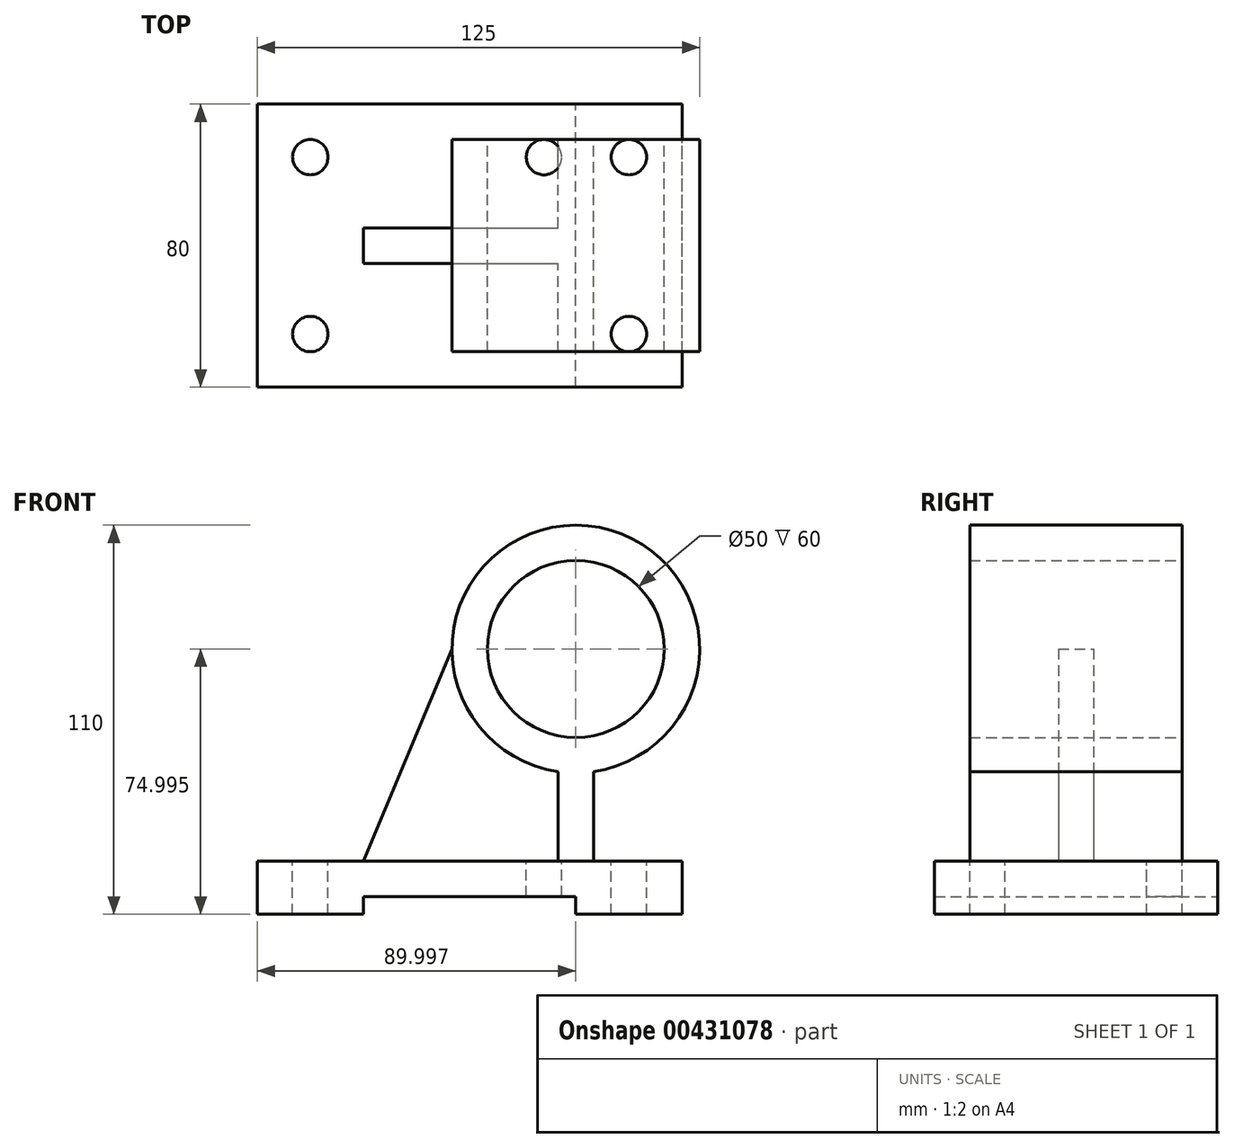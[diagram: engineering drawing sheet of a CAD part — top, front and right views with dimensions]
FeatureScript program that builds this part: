
annotation { "Feature Type Name" : "Feature", "Feature Type Description" : "" }
export const myFeature = defineFeature(function(context is Context, id is Id, definition is map)
    precondition{}
    {
        {
            var Q0;
            Q0=qCreatedBy(makeId("Front.planeOp"),FACE);
            var sketch = newSketch(context, id + "F0", { "sketchPlane" : qUnion([Q0])});
            skLineSegment(sketch, "E0.bottom", {"start": v(-48, -13.36) * mm, "end": v(72, -13.36) * mm});
            skLineSegment(sketch, "E0.top", {"start": v(-48, -28.36) * mm, "end": v(72, -28.36) * mm});
            skLineSegment(sketch, "E0.left", {"start": v(-48, -13.36) * mm, "end": v(-48, -28.36) * mm});
            skLineSegment(sketch, "E0.right", {"start": v(72, -13.36) * mm, "end": v(72, -28.36) * mm});
            skCircle(sketch, "E1", {"center": v(42, 46.64) * mm, "radius": 25 * mm});
            skCircle(sketch, "E2", {"center": v(42, 46.64) * mm, "radius": 35 * mm});
            skLineSegment(sketch, "E3", {"start": v(42, -13.36) * mm, "end": v(37, -13.36) * mm});
            skLineSegment(sketch, "E4", {"start": v(37, -13.36) * mm, "end": v(47, -13.36) * mm});
            skLineSegment(sketch, "E5", {"start": v(47, -13.36) * mm, "end": v(47, 12) * mm});
            skLineSegment(sketch, "E6", {"start": v(37, 12) * mm, "end": v(37, -13.36) * mm});
            skLineSegment(sketch, "E7.bottom", {"start": v(-18, -28.36) * mm, "end": v(42, -28.36) * mm});
            skLineSegment(sketch, "E7.top", {"start": v(-18, -23.36) * mm, "end": v(42, -23.36) * mm});
            skLineSegment(sketch, "E7.left", {"start": v(-18, -28.36) * mm, "end": v(-18, -23.36) * mm});
            skLineSegment(sketch, "E7.right", {"start": v(42, -28.36) * mm, "end": v(42, -23.36) * mm});
            skLineSegment(sketch, "E8", {"start": v(7, 46.64) * mm, "end": v(-18, -13.36) * mm});
            skLineSegment(sketch, "E9", {"start": v(-18, -13.36) * mm, "end": v(-48, -13.36) * mm});
            skPoint(sketch, "E10.start.orphan", {"position": v(47, 46.64) * mm});
            skSolve(sketch);
        }
        {
            var Q0;
            {var subQ6=sQuery(id+"F0.wireOp",EDGE,"E0.left");Q0=makeQuery(id+"F0.imprint","IMPRINT",FACE,{"disambiguationData":[TD([[makeQuery(id+"F0.imprint","IMPRINT",EDGE,{"derivedFrom":subQ6}),1.0]])]});}
            extrude(context, id + "F1", {"entities" : qUnion([Q0]), "depth" : 40 * mm, "hasSecondDirection" : true, "secondDirectionOppositeDirection" : true, "secondDirectionDepth" : 40 * mm});
        }
        {
            var Q0;
            {var subQ2=sQuery(id+"F0.wireOp",EDGE,"E6");Q0=makeQuery(id+"F0.imprint","IMPRINT",FACE,{"disambiguationData":[TD([[makeQuery(id+"F0.imprint","IMPRINT",EDGE,{"derivedFrom":subQ2}),-1.0]])]});}
            extrude(context, id + "F2", {"entities" : qUnion([Q0]), "operationType" : NewBodyOperationType.ADD, "depth" : 5 * mm, "hasSecondDirection" : true, "secondDirectionOppositeDirection" : true, "secondDirectionDepth" : 5 * mm});
        }
        {
            var Q0;
            Q0=makeQuery(id+"F0.imprint","IMPRINT",FACE,{"disambiguationData":[TD([[makeQuery(id+"F0.imprint","IMPRINT",EDGE,{"derivedFrom":sQuery(id+"F0.wireOp",EDGE,"E1")}),-1.0]])]});
            var Q1;
            {var subQ0=sQuery(id+"F0.wireOp",EDGE,"E5");Q1=makeQuery(id+"F0.imprint","IMPRINT",FACE,{"disambiguationData":[TD([[makeQuery(id+"F0.imprint","IMPRINT",EDGE,{"derivedFrom":subQ0}),1.0]])]});}
            extrude(context, id + "F3", {"entities" : qUnion([Q0, Q1]), "operationType" : NewBodyOperationType.ADD, "depth" : 30 * mm, "hasSecondDirection" : true, "secondDirectionOppositeDirection" : true, "secondDirectionDepth" : 30 * mm});
        }
        {
            var Q0;
            Q0=makeQuery(id+"F1.opExtrude","SWEPT_FACE",FACE,{"disambiguationData":[OSD([sQuery(id+"F0.wireOp",EDGE,"E0.bottom"),sQuery(id+"F0.wireOp",EDGE,"E4"),sQuery(id+"F0.wireOp",EDGE,"E9")])]});
            var sketch = newSketch(context, id + "F4", { "sketchPlane" : qUnion([Q0])});
            skLineSegment(sketch, "E11", {"start": v(-48, 40) * mm, "end": v(-33, 40) * mm});
            skLineSegment(sketch, "E12", {"start": v(-48, -40) * mm, "end": v(-33, -40) * mm});
            skLineSegment(sketch, "E13", {"start": v(-33, -40) * mm, "end": v(-33, -25) * mm});
            skCircle(sketch, "E14", {"center": v(-33, -25) * mm, "radius": 5 * mm});
            skLineSegment(sketch, "E15", {"start": v(-33, 40) * mm, "end": v(-33, 25) * mm});
            skCircle(sketch, "E16", {"center": v(-33, 25) * mm, "radius": 5 * mm});
            skLineSegment(sketch, "E17", {"start": v(72, 40) * mm, "end": v(42, 40) * mm});
            skLineSegment(sketch, "E18", {"start": v(72, -40) * mm, "end": v(42, -40) * mm});
            skCircle(sketch, "E19.MirrorC", {"center": v(33, 25) * mm, "radius": 5 * mm});
            skLineSegment(sketch, "E20", {"start": v(12, -40) * mm, "end": v(12, -30.6) * mm});
            skCircle(sketch, "E21.MirrorC", {"center": v(57, -25) * mm, "radius": 5 * mm});
            skCircle(sketch, "E22.MirrorC", {"center": v(57, 25) * mm, "radius": 5 * mm});
            skSolve(sketch);
        }
        {
            var Q0;
            Q0 = qSketchRegion(id + "F4", true);
            extrude(context, id + "F5", {"entities" : qUnion([Q0]), "operationType" : NewBodyOperationType.REMOVE, "oppositeDirection" : true, "depth" : 25 * mm});
        }
    });
